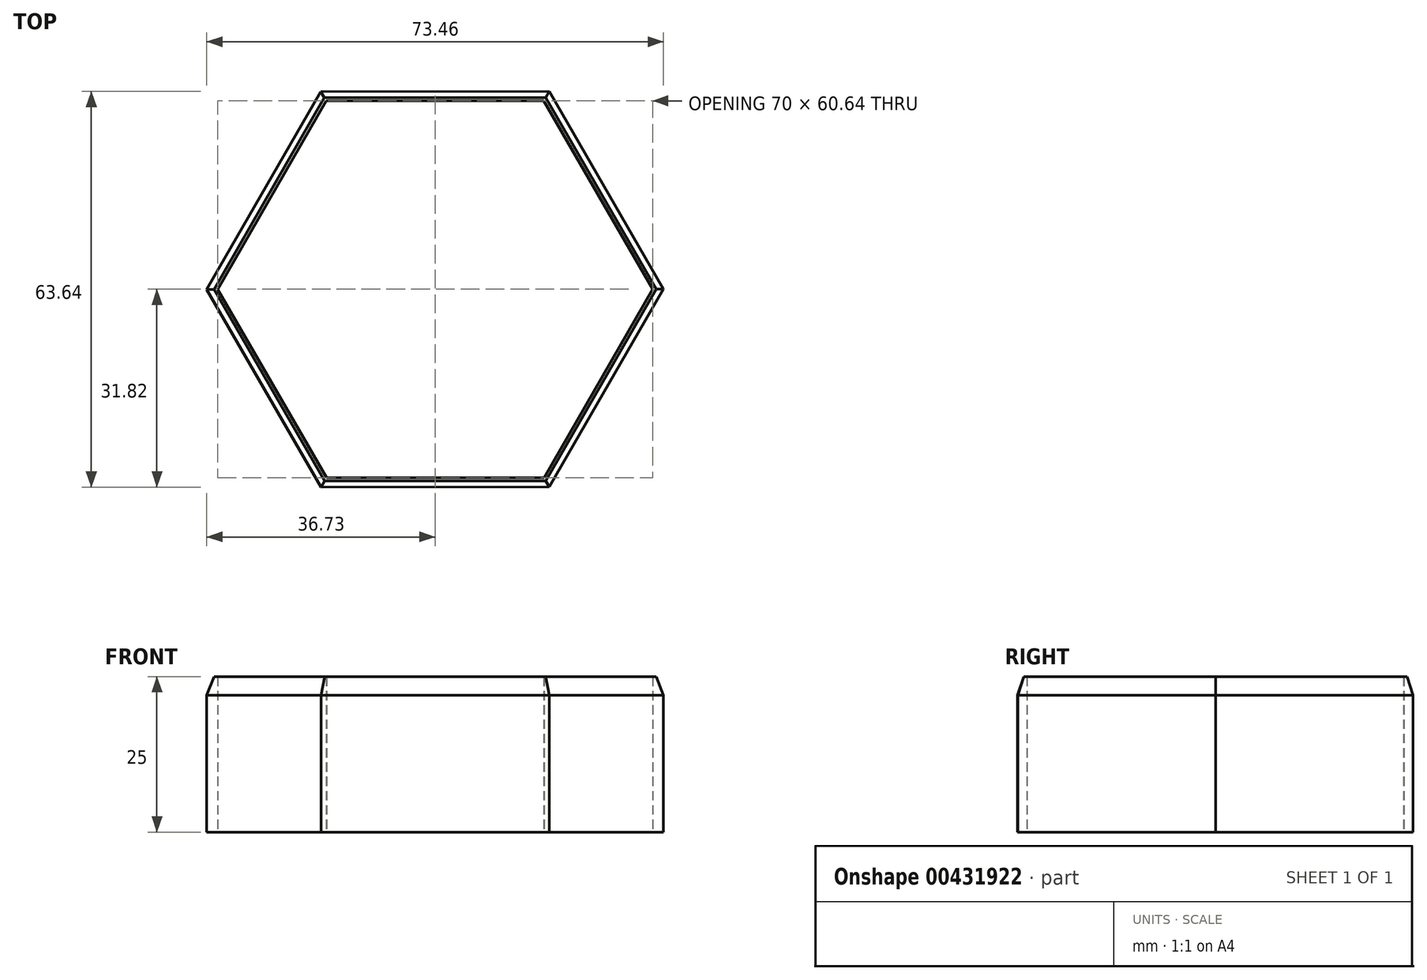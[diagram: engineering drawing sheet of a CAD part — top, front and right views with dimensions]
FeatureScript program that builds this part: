
annotation { "Feature Type Name" : "Feature", "Feature Type Description" : "" }
export const myFeature = defineFeature(function(context is Context, id is Id, definition is map)
    precondition{}
    {
        {
            var Q0;
            Q0=qCreatedBy(makeId("Top.planeOp"),FACE);
            var sketch = newSketch(context, id + "F0", { "sketchPlane" : qUnion([Q0])});
            skCircle(sketch, "E0.cCircle", {"center": v(0, 0) * mm, "radius": 30.31 * mm, "construction": true});
            skLineSegment(sketch, "E0.0", {"start": v(17.48, 30.32) * mm, "end": v(35, 0.02) * mm});
            skLineSegment(sketch, "E0.1", {"start": v(35, 0.02) * mm, "end": v(17.52, -30.3) * mm});
            skLineSegment(sketch, "E0.2", {"start": v(17.52, -30.3) * mm, "end": v(-17.48, -30.32) * mm});
            skLineSegment(sketch, "E0.3", {"start": v(-17.48, -30.32) * mm, "end": v(-35, -0.02) * mm});
            skLineSegment(sketch, "E0.4", {"start": v(-35, -0.02) * mm, "end": v(-17.52, 30.3) * mm});
            skLineSegment(sketch, "E0.5", {"start": v(-17.52, 30.3) * mm, "end": v(17.48, 30.32) * mm});
            skPoint(sketch, "E0.0.midPoint", {"position": v(26.24, 15.17) * mm});
            skLineSegment(sketch, "E1.0", {"start": v(-18.35, -31.82) * mm, "end": v(-36.73, -0.02) * mm});
            skLineSegment(sketch, "E1.1", {"start": v(-18.39, 31.8) * mm, "end": v(18.35, 31.82) * mm});
            skLineSegment(sketch, "E1.2", {"start": v(18.35, 31.82) * mm, "end": v(36.73, 0.02) * mm});
            skLineSegment(sketch, "E1.3", {"start": v(-36.73, -0.02) * mm, "end": v(-18.39, 31.8) * mm});
            skLineSegment(sketch, "E1.4", {"start": v(36.73, 0.02) * mm, "end": v(18.39, -31.8) * mm});
            skLineSegment(sketch, "E1.5", {"start": v(18.39, -31.8) * mm, "end": v(-18.35, -31.82) * mm});
            skSolve(sketch);
        }
        {
            var Q0;
            Q0 = qSketchRegion(id + "F0", true);
            extrude(context, id + "F1", {"entities" : qUnion([Q0]), "depth" : 25 * mm});
        }
        {
            var Q0;
            Q0=makeQuery(id+"F1.opExtrude","CAP_EDGE",EDGE,{"disambiguationData":[OSD([sQuery(id+"F0.wireOp",EDGE,"E1.4")])],"isStart":false});
            var Q1;
            Q1=makeQuery(id+"F1.opExtrude","CAP_EDGE",EDGE,{"disambiguationData":[OSD([sQuery(id+"F0.wireOp",EDGE,"E1.5")])],"isStart":false});
            var Q2;
            Q2=makeQuery(id+"F1.opExtrude","CAP_EDGE",EDGE,{"disambiguationData":[OSD([sQuery(id+"F0.wireOp",EDGE,"E1.0")])],"isStart":false});
            var Q3;
            Q3=makeQuery(id+"F1.opExtrude","CAP_EDGE",EDGE,{"disambiguationData":[OSD([sQuery(id+"F0.wireOp",EDGE,"E1.3")])],"isStart":false});
            var Q4;
            Q4=makeQuery(id+"F1.opExtrude","CAP_EDGE",EDGE,{"disambiguationData":[OSD([sQuery(id+"F0.wireOp",EDGE,"E1.1")])],"isStart":false});
            var Q5;
            Q5=makeQuery(id+"F1.opExtrude","CAP_EDGE",EDGE,{"disambiguationData":[OSD([sQuery(id+"F0.wireOp",EDGE,"E1.2")])],"isStart":false});
            chamfer(context, id + "F2", {"entities" : qUnion([Q0, Q1, Q2, Q3, Q4, Q5]), "chamferType" : ChamferType.TWO_OFFSETS, "width1" : 3 * mm, "oppositeDirection" : false, "width2" : 1 * mm, "tangentPropagation" : true});
        }
    });
